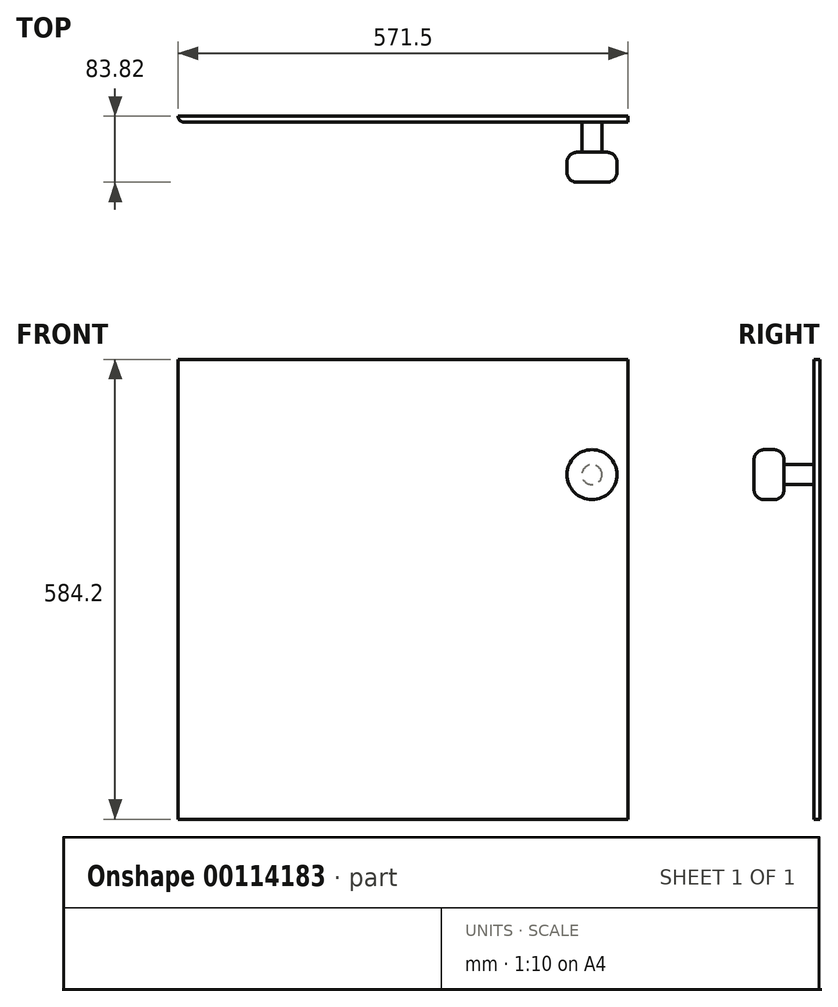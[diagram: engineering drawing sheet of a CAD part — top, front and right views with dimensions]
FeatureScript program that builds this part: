
annotation { "Feature Type Name" : "Feature", "Feature Type Description" : "" }
export const myFeature = defineFeature(function(context is Context, id is Id, definition is map)
    precondition{}
    {
        {
            var Q0;
            Q0=qCreatedBy(makeId("Front.planeOp"),FACE);
            var sketch = newSketch(context, id + "F0", { "sketchPlane" : qUnion([Q0])});
            skLineSegment(sketch, "E0.bottom", {"start": v(-303.53, 385.22) * mm, "end": v(267.97, 385.22) * mm});
            skLineSegment(sketch, "E0.top", {"start": v(-303.53, -198.98) * mm, "end": v(267.97, -198.98) * mm});
            skLineSegment(sketch, "E0.left", {"start": v(-303.53, 385.22) * mm, "end": v(-303.53, -198.98) * mm});
            skLineSegment(sketch, "E0.right", {"start": v(267.97, 385.22) * mm, "end": v(267.97, -198.98) * mm});
            skSolve(sketch);
        }
        {
            var Q0;
            Q0 = qSketchRegion(id + "F0", true);
            var Q1;
            Q1=makeQuery(id+"F0.imprint","IMPRINT",FACE,{"disambiguationData":[TD([[makeQuery(id+"F0.imprint","IMPRINT",EDGE,{"derivedFrom":sQuery(id+"F0.wireOp",EDGE,"E0.bottom")}),-1.0]])]});
            extrude(context, id + "F1", {"entities" : qUnion([Q0, Q1]), "depth" : 7.62 * mm});
        }
        {
            var Q0;
            Q0=makeQuery(id+"F1.opExtrude","CAP_EDGE",EDGE,{"disambiguationData":[OSD([sQuery(id+"F0.wireOp",EDGE,"E0.left")])],"isStart":false});
            fillet(context, id + "F2", {"entities" : qUnion([Q0]), "radius" : 7.62 * mm, "tangentPropagation" : true, "allowEdgeOverflow" : false});
        }
        {
            var Q0;
            Q0=makeQuery(id+"F1.opExtrude","CAP_FACE",FACE,{"disambiguationData":[OSD([sQuery(id+"F0.wireOp",EDGE,"E0.bottom"),sQuery(id+"F0.wireOp",EDGE,"E0.top"),sQuery(id+"F0.wireOp",EDGE,"E0.left"),sQuery(id+"F0.wireOp",EDGE,"E0.right")])],"isStart":false});
            var sketch = newSketch(context, id + "F3", { "sketchPlane" : qUnion([Q0])});
            skLineSegment(sketch, "E1", {"start": v(-295.9, 93.12) * mm, "end": v(267.97, 93.12) * mm});
            skCircle(sketch, "E2", {"center": v(222.1, 238.76) * mm, "radius": 12.7 * mm});
            skSolve(sketch);
        }
        {
            var Q0;
            Q0=makeQuery(id+"F3.imprint","IMPRINT",FACE,{"disambiguationData":[TD([[makeQuery(id+"F3.imprint","IMPRINT",EDGE,{"derivedFrom":sQuery(id+"F3.wireOp",EDGE,"E2")}),1.0]])]});
            extrude(context, id + "F4", {"entities" : qUnion([Q0]), "operationType" : NewBodyOperationType.ADD, "depth" : 38.1 * mm});
        }
        {
            var Q0;
            Q0=makeQuery(id+"F4.opExtrude","CAP_FACE",FACE,{"disambiguationData":[OSD([sQuery(id+"F3.wireOp",EDGE,"E2")])],"isStart":false});
            var sketch = newSketch(context, id + "F5", { "sketchPlane" : qUnion([Q0])});
            skCircle(sketch, "E3", {"center": v(222.1, 238.76) * mm, "radius": 31.75 * mm});
            skSolve(sketch);
        }
        {
            var Q0;
            Q0=makeQuery(id+"F5.imprint","IMPRINT",FACE,{"disambiguationData":[TD([[makeQuery(id+"F5.imprint","IMPRINT",EDGE,{"derivedFrom":makeQuery(id+"F4.opExtrude","CAP_EDGE",EDGE,{"disambiguationData":[OSD([sQuery(id+"F3.wireOp",EDGE,"E2")])],"isStart":false})}),1.0]])]});
            var Q1;
            Q1=makeQuery(id+"F5.imprint","IMPRINT",FACE,{"disambiguationData":[TD([[makeQuery(id+"F5.imprint","IMPRINT",EDGE,{"derivedFrom":sQuery(id+"F5.wireOp",EDGE,"E3")}),1.0]])]});
            var Q2;
            Q2=makeQuery(id+"F5.imprint","IMPRINT",FACE,{"disambiguationData":[TD([[makeQuery(id+"F5.imprint","IMPRINT",EDGE,{"derivedFrom":sQuery(id+"F5.wireOp",EDGE,"E3")}),1.0]])]});
            extrude(context, id + "F6", {"entities" : qUnion([Q0, Q1, Q2]), "operationType" : NewBodyOperationType.ADD, "depth" : 38.1 * mm});
        }
        {
            var Q0;
            Q0=makeQuery(id+"F6.opExtrude","CAP_EDGE",EDGE,{"disambiguationData":[OSD([sQuery(id+"F5.wireOp",EDGE,"E3")])],"isStart":false});
            var Q1;
            Q1=makeQuery(id+"F6.opExtrude","CAP_EDGE",EDGE,{"disambiguationData":[OSD([sQuery(id+"F5.wireOp",EDGE,"E3")])],"isStart":true});
            fillet(context, id + "F7", {"entities" : qUnion([Q0, Q1]), "radius" : 12.7 * mm, "tangentPropagation" : true, "allowEdgeOverflow" : false});
        }
    });
